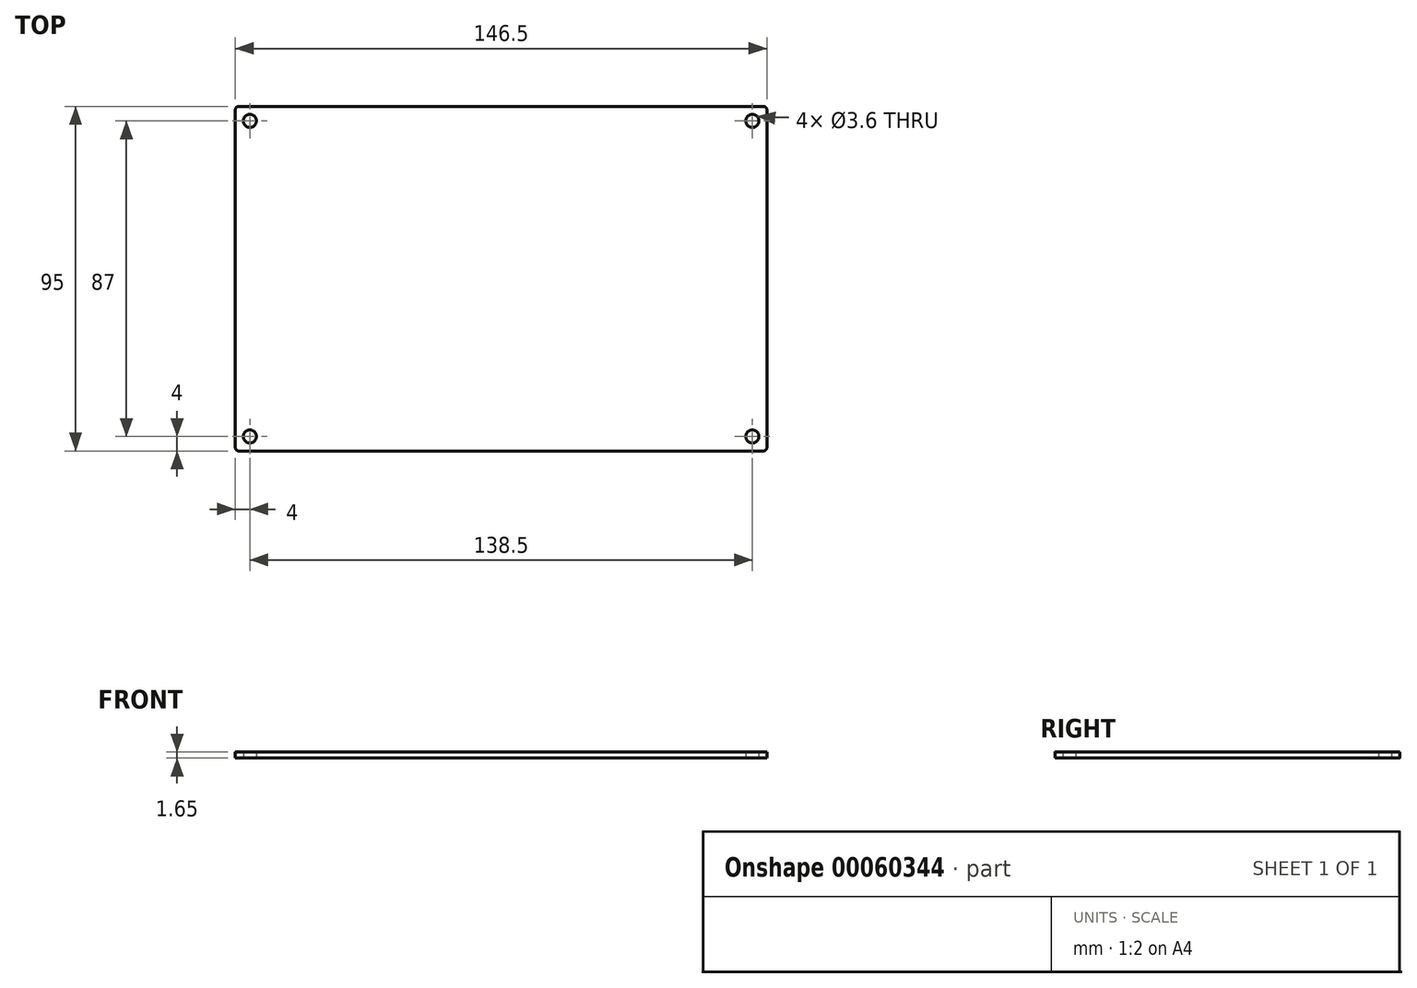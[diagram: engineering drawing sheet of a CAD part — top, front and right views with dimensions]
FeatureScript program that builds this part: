
annotation { "Feature Type Name" : "Feature", "Feature Type Description" : "" }
export const myFeature = defineFeature(function(context is Context, id is Id, definition is map)
    precondition{}
    {
        {
            var Q0;
            Q0=qCreatedBy(makeId("Top.planeOp"),FACE);
            var sketch = newSketch(context, id + "F0", { "sketchPlane" : qUnion([Q0])});
            skLineSegment(sketch, "E0.bottom", {"start": v(-72.25, 47.5) * mm, "end": v(72.25, 47.5) * mm});
            skLineSegment(sketch, "E0.top", {"start": v(-72.25, -47.5) * mm, "end": v(72.25, -47.5) * mm});
            skLineSegment(sketch, "E0.left", {"start": v(-73.25, 46.5) * mm, "end": v(-73.25, -46.5) * mm});
            skLineSegment(sketch, "E0.right", {"start": v(73.25, 46.5) * mm, "end": v(73.25, -46.5) * mm});
            skCircle(sketch, "E1", {"center": v(-69.25, 43.5) * mm, "radius": 1.8 * mm});
            skCircle(sketch, "E2", {"center": v(-69.25, -43.5) * mm, "radius": 1.8 * mm});
            skCircle(sketch, "E3", {"center": v(69.25, -43.5) * mm, "radius": 1.8 * mm});
            skCircle(sketch, "E4", {"center": v(69.25, 43.5) * mm, "radius": 1.8 * mm});
            skPoint(sketch, "E5.visualSharp", {"position": v(-73.25, 47.5) * mm});
            skArc(sketch, "E5.filletArc", {"start": v(-72.25, 47.5) * mm, "mid": v(-72.96, 47.2) * mm, "end": v(-73.25, 46.5) * mm});
            skPoint(sketch, "E6.visualSharp", {"position": v(73.25, 47.5) * mm});
            skArc(sketch, "E6.filletArc", {"start": v(73.25, 46.5) * mm, "mid": v(72.96, 47.2) * mm, "end": v(72.25, 47.5) * mm});
            skPoint(sketch, "E7.visualSharp", {"position": v(73.25, -47.5) * mm});
            skArc(sketch, "E7.filletArc", {"start": v(72.25, -47.5) * mm, "mid": v(72.96, -47.2) * mm, "end": v(73.25, -46.5) * mm});
            skPoint(sketch, "E8.visualSharp", {"position": v(-73.25, -47.5) * mm});
            skArc(sketch, "E8.filletArc", {"start": v(-73.25, -46.5) * mm, "mid": v(-72.96, -47.2) * mm, "end": v(-72.25, -47.5) * mm});
            skSolve(sketch);
        }
        {
            var Q0;
            Q0 = qSketchRegion(id + "F0", true);
            extrude(context, id + "F1", {"entities" : qUnion([Q0]), "depth" : 1.65 * mm});
        }
    });
